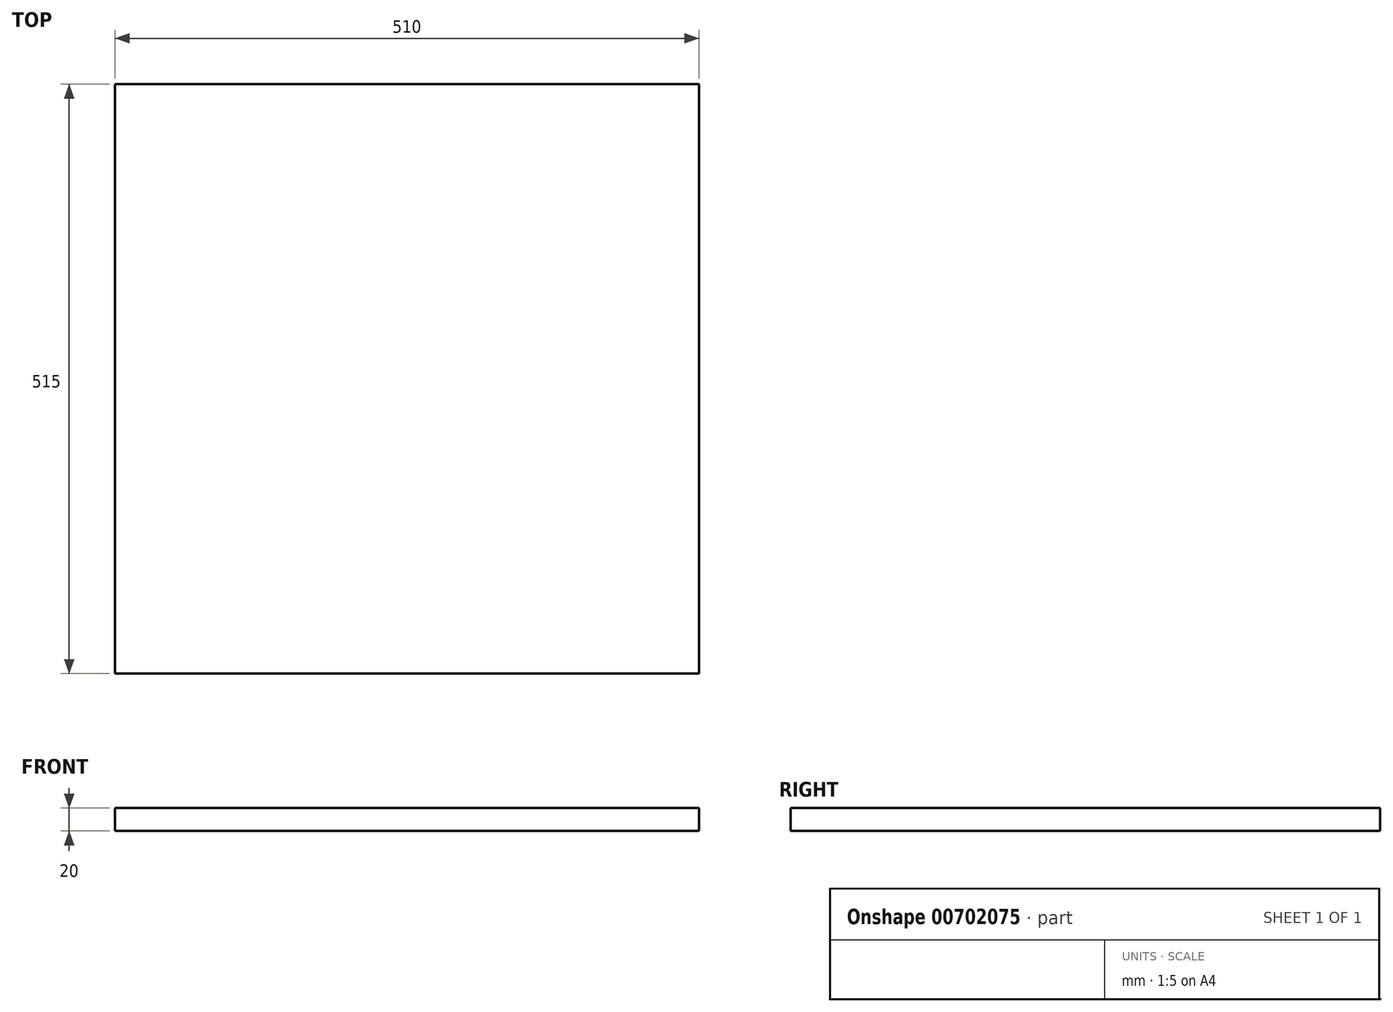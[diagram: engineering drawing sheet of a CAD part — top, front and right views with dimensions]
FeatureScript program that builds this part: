
annotation { "Feature Type Name" : "Feature", "Feature Type Description" : "" }
export const myFeature = defineFeature(function(context is Context, id is Id, definition is map)
    precondition{}
    {
        {
            var Q0;
            Q0=qCreatedBy(makeId("Top.planeOp"),FACE);
            var sketch = newSketch(context, id + "F0", { "sketchPlane" : qUnion([Q0])});
            skLineSegment(sketch, "E0.bottom", {"start": v(0, 0) * mm, "end": v(510, 0) * mm});
            skLineSegment(sketch, "E0.top", {"start": v(0, 515) * mm, "end": v(510, 515) * mm});
            skLineSegment(sketch, "E0.left", {"start": v(0, 0) * mm, "end": v(0, 515) * mm});
            skLineSegment(sketch, "E0.right", {"start": v(510, 0) * mm, "end": v(510, 515) * mm});
            skSolve(sketch);
        }
        {
            var Q0;
            Q0=makeQuery(id+"F0.imprint","IMPRINT",FACE,{"disambiguationData":[TD([[makeQuery(id+"F0.imprint","IMPRINT",EDGE,{"derivedFrom":sQuery(id+"F0.wireOp",EDGE,"E0.bottom")}),1.0]])]});
            extrude(context, id + "F1", {"entities" : qUnion([Q0]), "depth" : 20 * mm, "offsetDistance" : 25 * mm});
        }
    });
